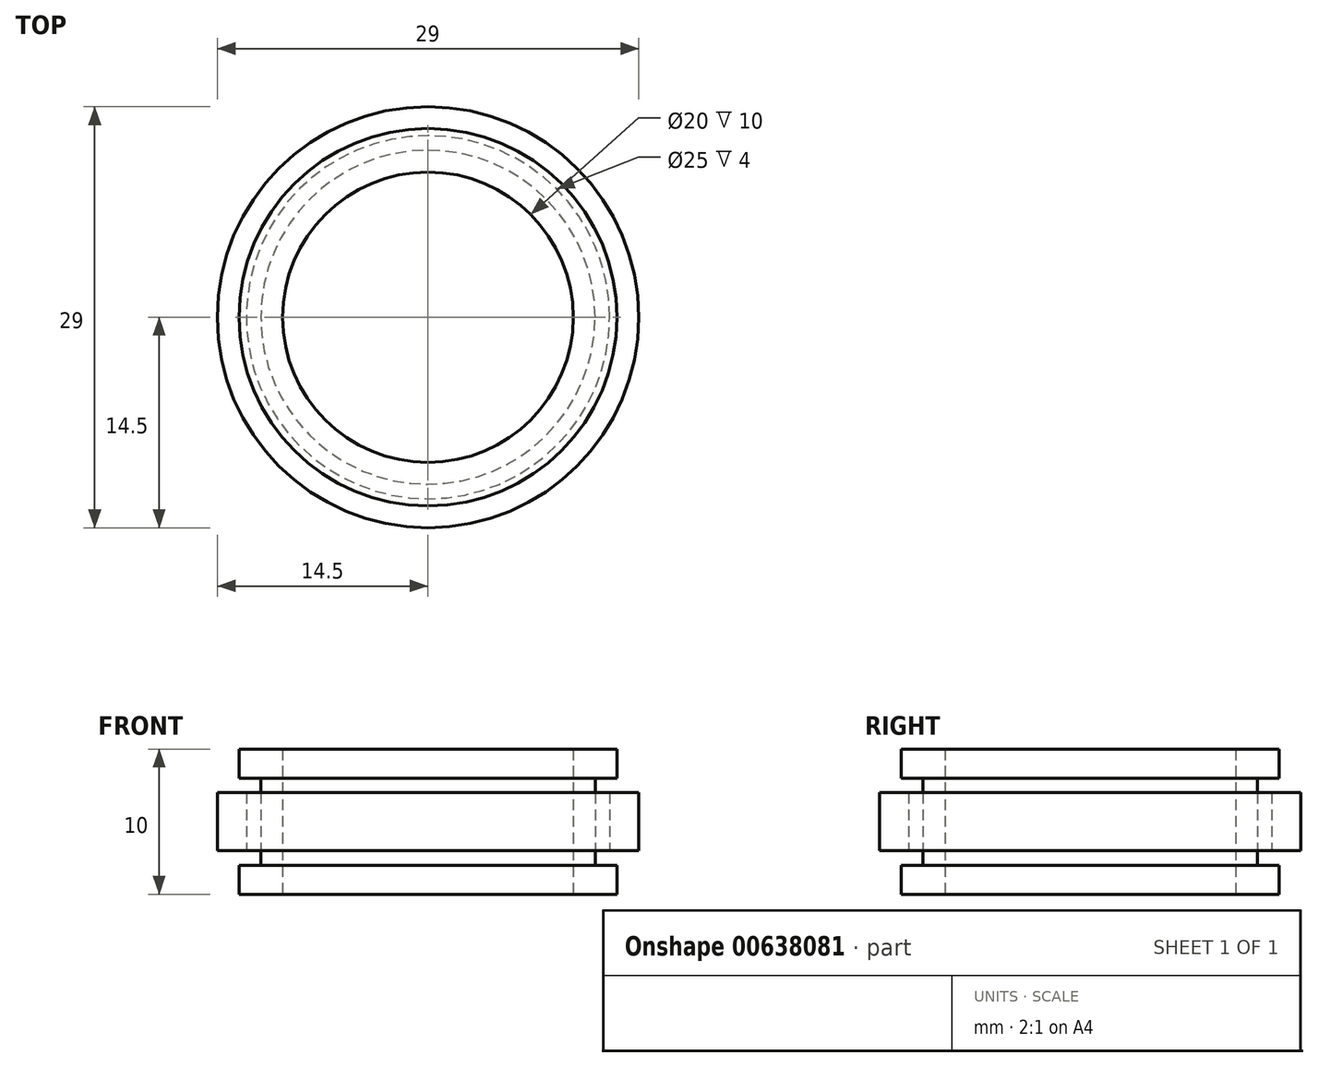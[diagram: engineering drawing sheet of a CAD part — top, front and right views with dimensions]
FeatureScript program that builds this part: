
annotation { "Feature Type Name" : "Feature", "Feature Type Description" : "" }
export const myFeature = defineFeature(function(context is Context, id is Id, definition is map)
    precondition{}
    {
        {
            var Q0;
            Q0=qCreatedBy(makeId("Front.planeOp"),FACE);
            var sketch = newSketch(context, id + "F0", { "sketchPlane" : qUnion([Q0])});
            skLineSegment(sketch, "E0", {"start": v(-10, 0) * mm, "end": v(-10, 6) * mm});
            skLineSegment(sketch, "E1", {"start": v(-10, 6) * mm, "end": v(-11.5, 6) * mm});
            skLineSegment(sketch, "E2", {"start": v(-11.5, 6) * mm, "end": v(-11.5, 0) * mm});
            skLineSegment(sketch, "E3", {"start": v(-11.5, 0) * mm, "end": v(-10, 0) * mm});
            skLineSegment(sketch, "E4", {"start": v(-10, 6) * mm, "end": v(-10, 8) * mm});
            skLineSegment(sketch, "E5", {"start": v(-10, 8) * mm, "end": v(-13, 8) * mm});
            skLineSegment(sketch, "E6", {"start": v(-13, 8) * mm, "end": v(-13, 6) * mm});
            skLineSegment(sketch, "E7", {"start": v(-13, 6) * mm, "end": v(-11.5, 6) * mm});
            skLineSegment(sketch, "E8", {"start": v(-10, 0) * mm, "end": v(-10, -2) * mm});
            skLineSegment(sketch, "E9", {"start": v(-10, -2) * mm, "end": v(-13, -2) * mm});
            skLineSegment(sketch, "E10", {"start": v(-13, -2) * mm, "end": v(-13, 0) * mm});
            skLineSegment(sketch, "E11", {"start": v(-13, 0) * mm, "end": v(-11.5, 0) * mm});
            skLineSegment(sketch, "E12", {"start": v(0, 0.76) * mm, "end": v(0, 6.56) * mm});
            skLineSegment(sketch, "E13", {"start": v(-14.5, 5) * mm, "end": v(-14.5, 1) * mm});
            skLineSegment(sketch, "E14", {"start": v(-14.5, 1) * mm, "end": v(-12.5, 1) * mm});
            skLineSegment(sketch, "E15", {"start": v(-12.5, 1) * mm, "end": v(-12.5, 5) * mm});
            skLineSegment(sketch, "E16", {"start": v(-12.5, 5) * mm, "end": v(-14.5, 5) * mm});
            skSolve(sketch);
        }
        {
            var Q0;
            Q0=makeQuery(id+"F0.imprint","IMPRINT",FACE,{"disambiguationData":[TD([[makeQuery(id+"F0.imprint","IMPRINT",EDGE,{"derivedFrom":sQuery(id+"F0.wireOp",EDGE,"E1")}),-1.0]])]});
            var Q1;
            Q1=makeQuery(id+"F0.imprint","IMPRINT",FACE,{"disambiguationData":[TD([[makeQuery(id+"F0.imprint","IMPRINT",EDGE,{"derivedFrom":sQuery(id+"F0.wireOp",EDGE,"E0")}),1.0]])]});
            var Q2;
            Q2=makeQuery(id+"F0.imprint","IMPRINT",FACE,{"disambiguationData":[TD([[makeQuery(id+"F0.imprint","IMPRINT",EDGE,{"derivedFrom":sQuery(id+"F0.wireOp",EDGE,"E3")}),-1.0]])]});
            var Q3;
            Q3=makeQuery(id+"F0.imprint","IMPRINT",FACE,{"disambiguationData":[TD([[makeQuery(id+"F0.imprint","IMPRINT",EDGE,{"derivedFrom":sQuery(id+"F0.wireOp",EDGE,"E13")}),1.0]])]});
            var Q4;
            Q4=sQuery(id+"F0.wireOp",EDGE,"E12");
            revolve(context, id + "F1", {"entities" : qUnion([Q0, Q1, Q2, Q3]), "axis" : qUnion([Q4]), "revolveType" : RevolveType.FULL});
        }
    });
